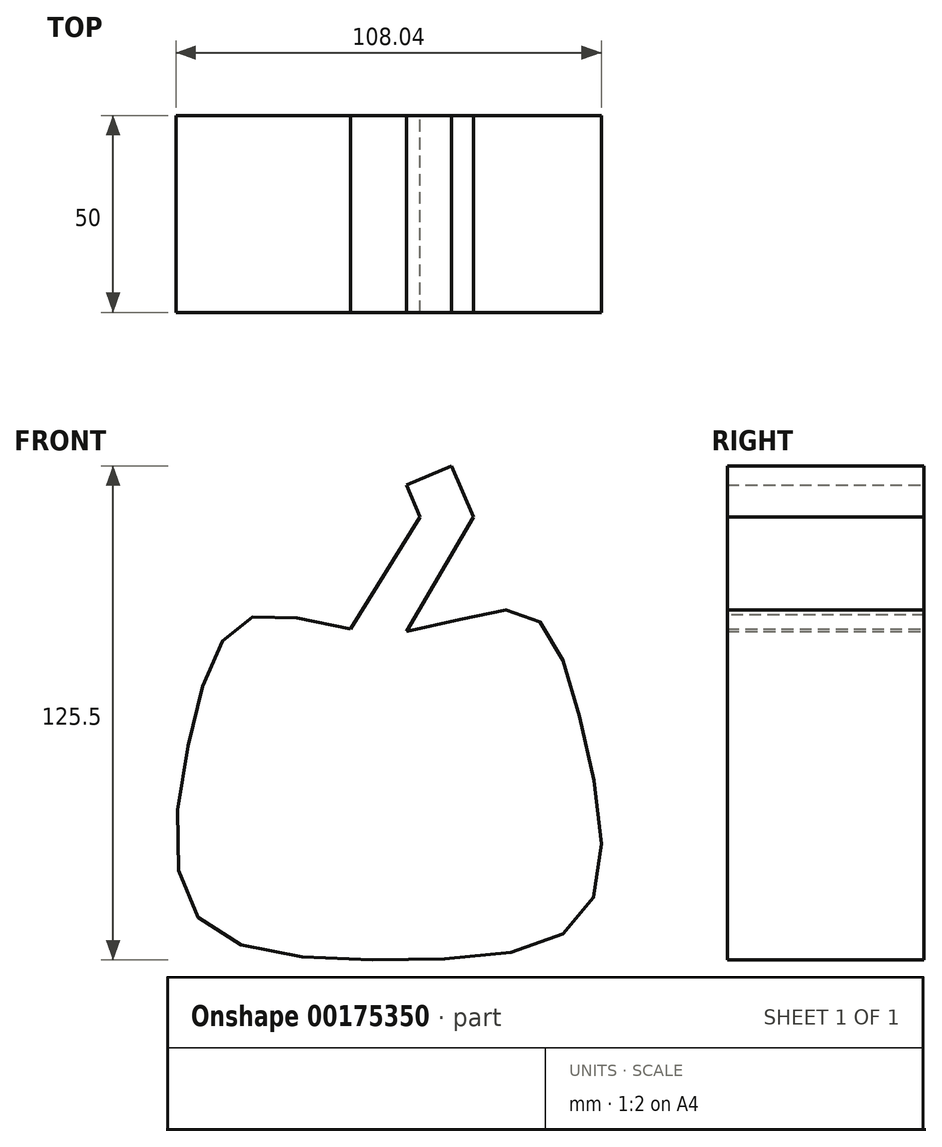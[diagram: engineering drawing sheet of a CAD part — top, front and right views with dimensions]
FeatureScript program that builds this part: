
annotation { "Feature Type Name" : "Feature", "Feature Type Description" : "" }
export const myFeature = defineFeature(function(context is Context, id is Id, definition is map)
    precondition{}
    {
        {
            var Q0;
            Q0=qCreatedBy(makeId("Front.planeOp"),FACE);
            var sketch = newSketch(context, id + "F0", { "sketchPlane" : qUnion([Q0])});
            skFitSpline(sketch, "E0", {"points": [v(-51.23, 0) * mm, v(-36.55, 27.63) * mm, v(0, 23.89) * mm, v(33.1, 29.07) * mm, v(47.78, 0) * mm, v(48.35, -47.78) * mm, v(0, -59.29) * mm, v(-50.37, -47.78) * mm, v(-51.23, 0) * mm]});
            skLineSegment(sketch, "E1", {"start": v(-11.03, 24.84) * mm, "end": v(6.61, 53.22) * mm});
            skLineSegment(sketch, "E2", {"start": v(6.61, 53.22) * mm, "end": v(3.17, 61.3) * mm});
            skLineSegment(sketch, "E3", {"start": v(3.17, 61.3) * mm, "end": v(14.64, 66.2) * mm});
            skLineSegment(sketch, "E4", {"start": v(14.64, 66.2) * mm, "end": v(20.17, 53.22) * mm});
            skLineSegment(sketch, "E5", {"start": v(20.17, 53.22) * mm, "end": v(3.17, 24.13) * mm});
            skSolve(sketch);
        }
        {
            var Q0;
            Q0 = qSketchRegion(id + "F0", true);
            extrude(context, id + "F1", {"entities" : qUnion([Q0]), "depth" : 50 * mm});
        }
    });
